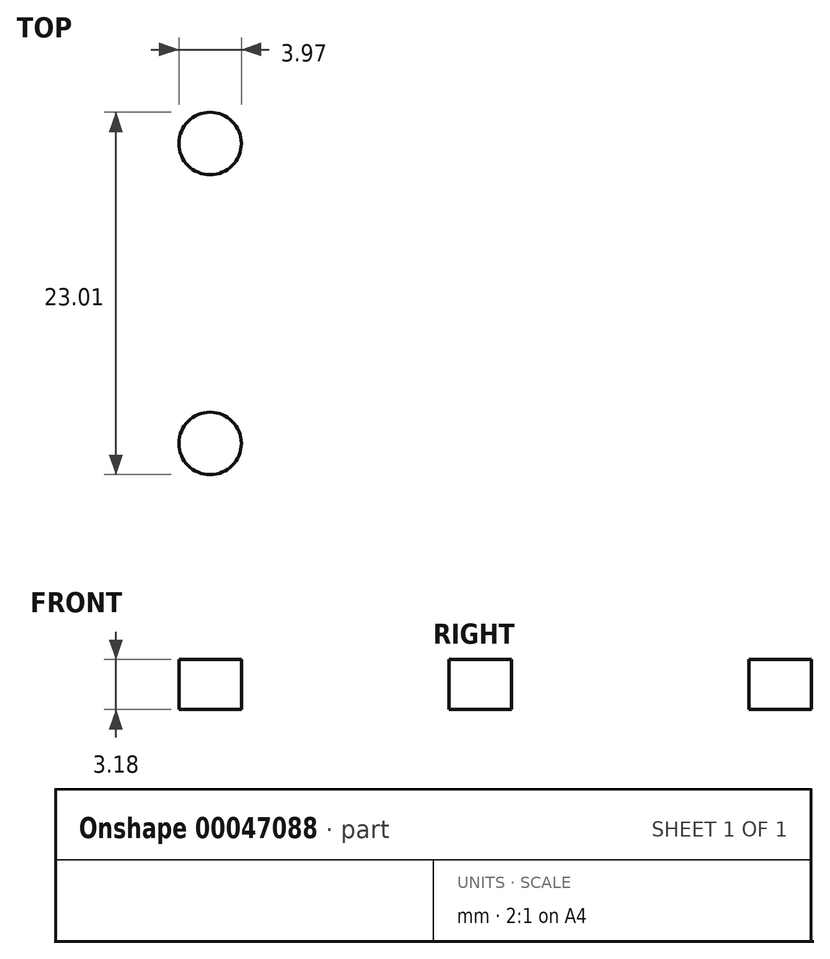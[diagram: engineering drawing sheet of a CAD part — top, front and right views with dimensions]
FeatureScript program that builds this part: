
annotation { "Feature Type Name" : "Feature", "Feature Type Description" : "" }
export const myFeature = defineFeature(function(context is Context, id is Id, definition is map)
    precondition{}
    {
        {
            var Q0;
            Q0=qCreatedBy(makeId("Top.planeOp"),FACE);
            var sketch = newSketch(context, id + "F0", { "sketchPlane" : qUnion([Q0])});
            skLineSegment(sketch, "E0.rect.bottom", {"start": v(9.53, 38.1) * mm, "end": v(-9.52, 38.1) * mm});
            skLineSegment(sketch, "E0.rect.top", {"start": v(9.52, -38.1) * mm, "end": v(-9.53, -38.1) * mm});
            skLineSegment(sketch, "E0.rect.left", {"start": v(9.53, 38.1) * mm, "end": v(9.52, -38.1) * mm});
            skLineSegment(sketch, "E0.rect.right", {"start": v(-9.52, 38.1) * mm, "end": v(-9.53, -38.1) * mm});
            skPoint(sketch, "E0.rect.middle", {"position": v(0, 0) * mm});
            skSolve(sketch);
        }
        {
            var Q0;
            Q0=makeQuery(id+"F0.imprint","IMPRINT",FACE,{"disambiguationData":[TD([[makeQuery(id+"F0.imprint","IMPRINT",EDGE,{"derivedFrom":sQuery(id+"F0.wireOp",EDGE,"E0.rect.bottom")}),1.0]])]});
            extrude(context, id + "F1", {"entities" : qUnion([Q0]), "endBound" : BoundingType.SYMMETRIC, "depth" : 3.17 * mm});
        }
        {
            var Q0;
            Q0=makeQuery(id+"F1.opExtrude","CAP_FACE",FACE,{"disambiguationData":[OSD([sQuery(id+"F0.wireOp",EDGE,"E0.rect.bottom"),sQuery(id+"F0.wireOp",EDGE,"E0.rect.top"),sQuery(id+"F0.wireOp",EDGE,"E0.rect.left"),sQuery(id+"F0.wireOp",EDGE,"E0.rect.right")])],"isStart":false});
            var sketch = newSketch(context, id + "F2", { "sketchPlane" : qUnion([Q0])});
            skLineSegment(sketch, "E1", {"start": v(0, -38.1) * mm, "end": v(0, 25.4) * mm, "construction": true});
            skPoint(sketch, "E1.endSnap0", {"position": v(0, -38.1) * mm});
            skLineSegment(sketch, "E2", {"start": v(9.52, -38.1) * mm, "end": v(3.17, -38.1) * mm, "construction": true});
            skLineSegment(sketch, "E3", {"start": v(3.17, -38.1) * mm, "end": v(3.17, 6.35) * mm, "construction": true});
            skCircle(sketch, "E4", {"center": v(3.17, 6.35) * mm, "radius": 1.98 * mm});
            skLineSegment(sketch, "E5", {"start": v(0, 25.4) * mm, "end": v(3.17, 25.4) * mm, "construction": true});
            skCircle(sketch, "E6", {"center": v(3.17, 25.4) * mm, "radius": 1.98 * mm});
            skCircle(sketch, "E7.MirrorC", {"center": v(-3.17, 25.4) * mm, "radius": 1.98 * mm});
            skCircle(sketch, "E8.MirrorC", {"center": v(-3.17, 6.35) * mm, "radius": 1.98 * mm});
            skSolve(sketch);
        }
        {
            var Q0;
            Q0=makeQuery(id+"F2.imprint","IMPRINT",FACE,{"disambiguationData":[TD([[makeQuery(id+"F2.imprint","IMPRINT",EDGE,{"derivedFrom":sQuery(id+"F2.wireOp",EDGE,"E6")}),1.0]])]});
            var Q1;
            Q1=makeQuery(id+"F2.imprint","IMPRINT",FACE,{"disambiguationData":[TD([[makeQuery(id+"F2.imprint","IMPRINT",EDGE,{"derivedFrom":sQuery(id+"F2.wireOp",EDGE,"E7.MirrorC")}),-1.0]])]});
            var Q2;
            Q2=makeQuery(id+"F2.imprint","IMPRINT",FACE,{"disambiguationData":[TD([[makeQuery(id+"F2.imprint","IMPRINT",EDGE,{"derivedFrom":sQuery(id+"F2.wireOp",EDGE,"E8.MirrorC")}),-1.0]])]});
            var Q3;
            Q3=makeQuery(id+"F2.imprint","IMPRINT",FACE,{"disambiguationData":[TD([[makeQuery(id+"F2.imprint","IMPRINT",EDGE,{"derivedFrom":sQuery(id+"F2.wireOp",EDGE,"E4")}),1.0]])]});
            extrude(context, id + "F3", {"entities" : qUnion([Q0, Q1, Q2, Q3]), "operationType" : NewBodyOperationType.REMOVE, "endBound" : BoundingType.UP_TO_NEXT, "oppositeDirection" : true, "depth" : 25.4 * mm});
        }
    });
